# Revit family: 29301
name_source: partatom
category: Plumbing Fixtures
units: mm (PartAtom-declared; Revit-internal decimal feet)

## family parameters
Always vertical = Yes
Cut with Voids When Loaded = No
Maintain Annotation Orientation = No
OmniClass Number = 23.45.00.00
OmniClass Title = Sanitary, Laundry, and Cleaning Equipment
Part Type = Normal
Room Calculation Point = No
Round Connector Dimension = Use Diameter
Shared = No
Work Plane-Based = Yes

## types (1)
- 29301-presto
    - Hydraulic supply = 12.5 "
    -Delivered with = Instruction manual
    > Standards & approvals = Brass body in accordance with EN 1982, EN 12164, EN 12156
    > Thermal resistance : = 75.0000 (h·ft²·°F)/BTU
    Default Elevation = 1219 mm
    Description = Fixed shower head
    Model = 29301
    Recommended pressure = 3.00 bar
    URL = https://www.prestodatashare.com
    brand = LES ROBINETS PRESTO
    flow = 3 L/min
    min pressure = 1.00 bar
    power = 0 VA
    pressure = 5.00 bar
    range = Shower heads

## geometry (parser evidence)
native form markers: Sweep x3
no freeform markers — native parametric forms only
